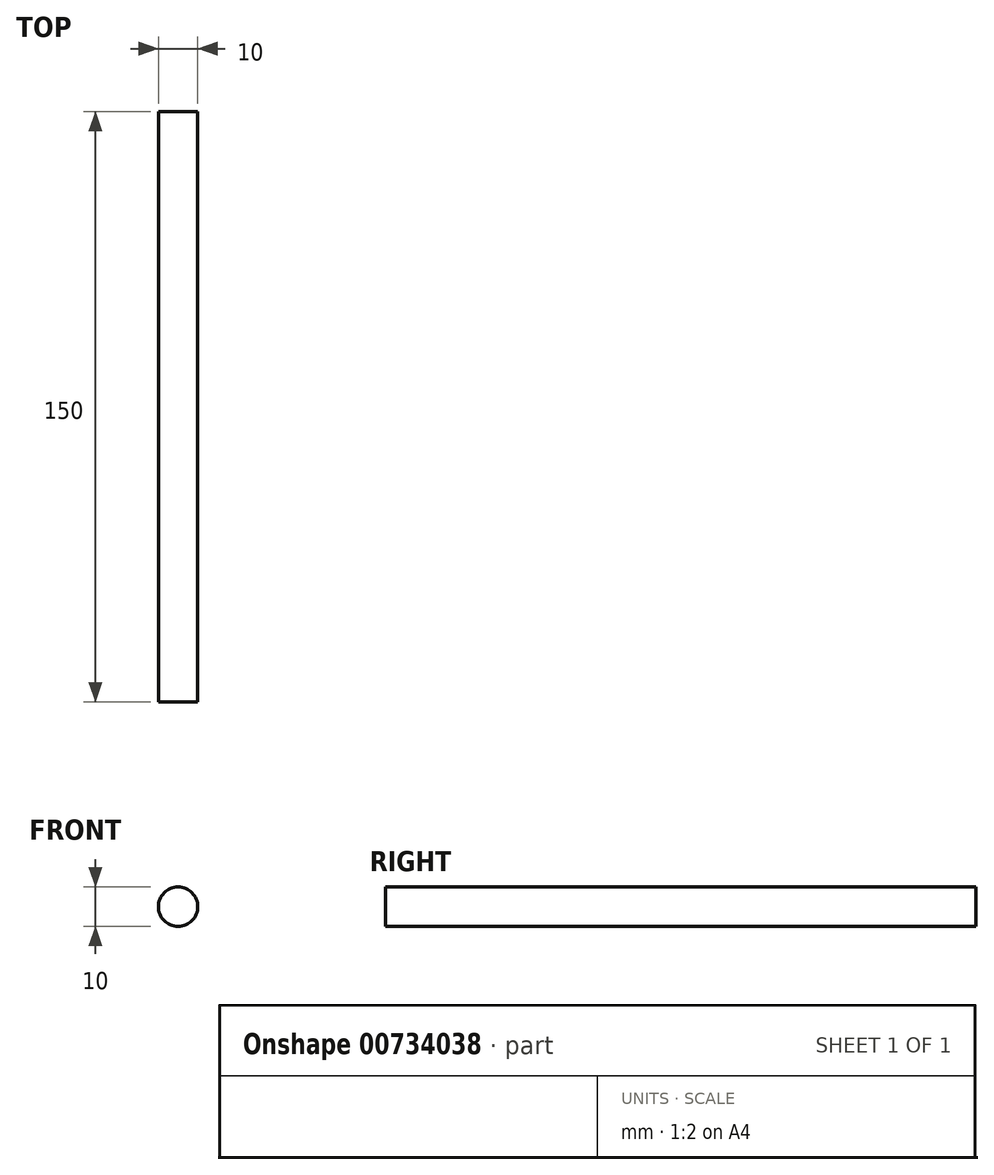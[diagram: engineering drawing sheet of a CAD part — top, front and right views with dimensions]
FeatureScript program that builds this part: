
annotation { "Feature Type Name" : "Feature", "Feature Type Description" : "" }
export const myFeature = defineFeature(function(context is Context, id is Id, definition is map)
    precondition{}
    {
        {
            var Q0;
            Q0=qCreatedBy(makeId("Front.planeOp"),FACE);
            var sketch = newSketch(context, id + "F0", { "sketchPlane" : qUnion([Q0])});
            skCircle(sketch, "E0", {"center": v(-77.05, 7.15) * mm, "radius": 5 * mm});
            skSolve(sketch);
        }
        {
            var Q0;
            Q0=qSketchRegion(id+"F0",true);
            extrude(context, id + "F1", {"entities" : qUnion([Q0]), "depth" : 150 * mm, "offsetDistance" : 25 * mm});
        }
    });
